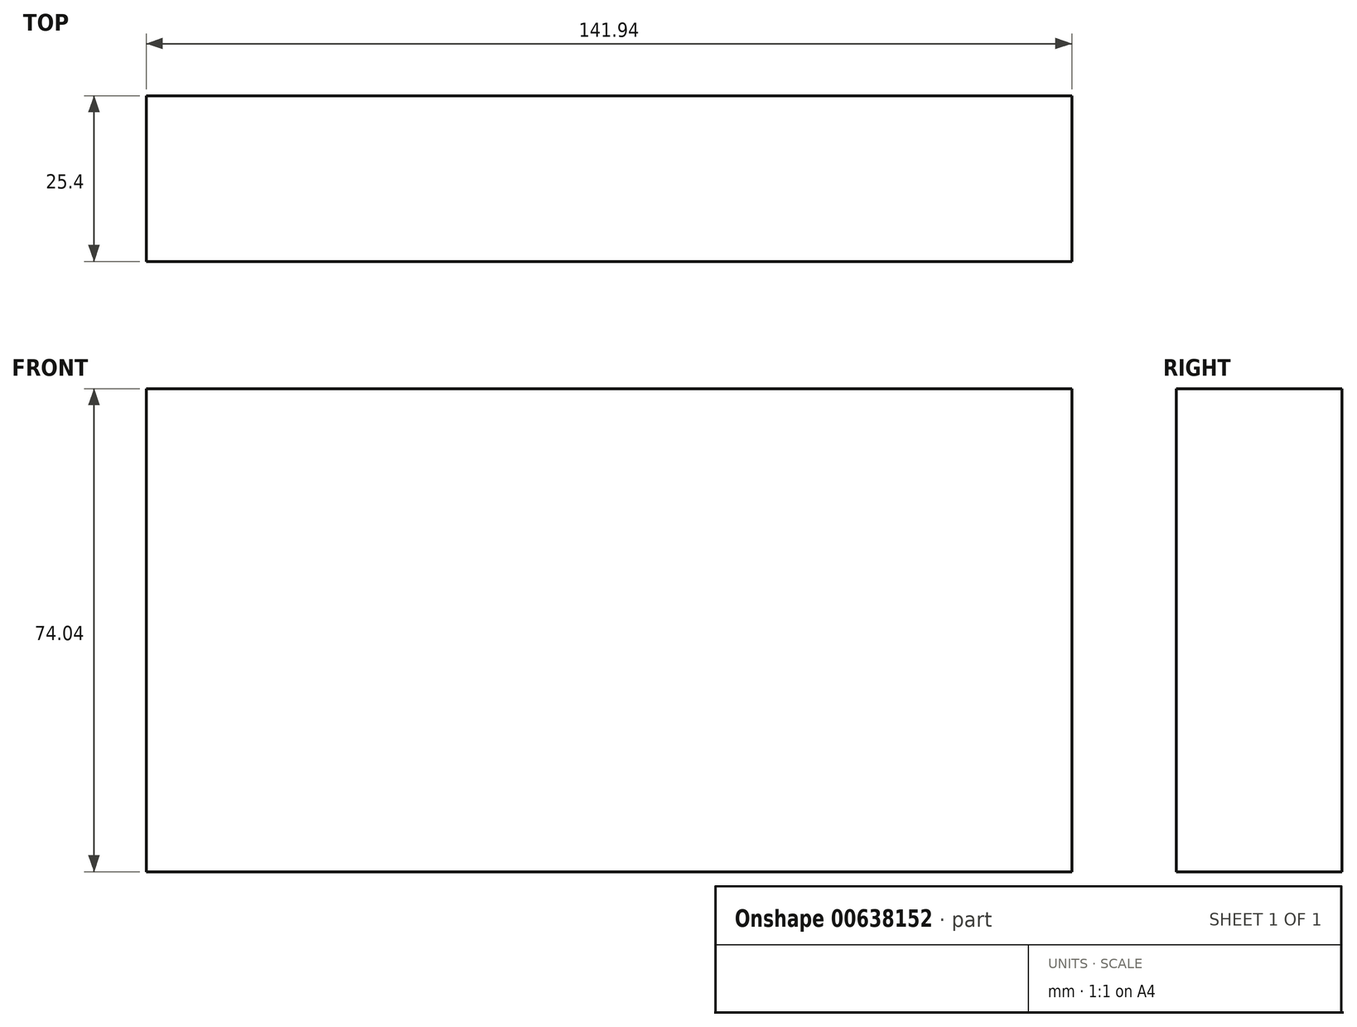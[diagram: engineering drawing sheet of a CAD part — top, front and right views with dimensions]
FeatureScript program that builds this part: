
annotation { "Feature Type Name" : "Feature", "Feature Type Description" : "" }
export const myFeature = defineFeature(function(context is Context, id is Id, definition is map)
    precondition{}
    {
        {
            var Q0;
            Q0=qCreatedBy(makeId("Front.planeOp"),FACE);
            var sketch = newSketch(context, id + "F0", { "sketchPlane" : qUnion([Q0])});
            skLineSegment(sketch, "E0.bottom", {"start": v(70.97, -37.02) * mm, "end": v(-70.97, -37.02) * mm});
            skLineSegment(sketch, "E0.top", {"start": v(70.97, 37.02) * mm, "end": v(-70.97, 37.02) * mm});
            skLineSegment(sketch, "E0.left", {"start": v(70.97, -37.02) * mm, "end": v(70.97, 37.02) * mm});
            skLineSegment(sketch, "E0.right", {"start": v(-70.97, -37.02) * mm, "end": v(-70.97, 37.02) * mm});
            skPoint(sketch, "E0.middle", {"position": v(0, 0) * mm});
            skSolve(sketch);
        }
        {
            var Q0;
            Q0 = qSketchRegion(id + "F0", true);
            extrude(context, id + "F1", {"entities" : qUnion([Q0]), "depth" : 25.4 * mm, "offsetDistance" : 25.4 * mm});
        }
    });
